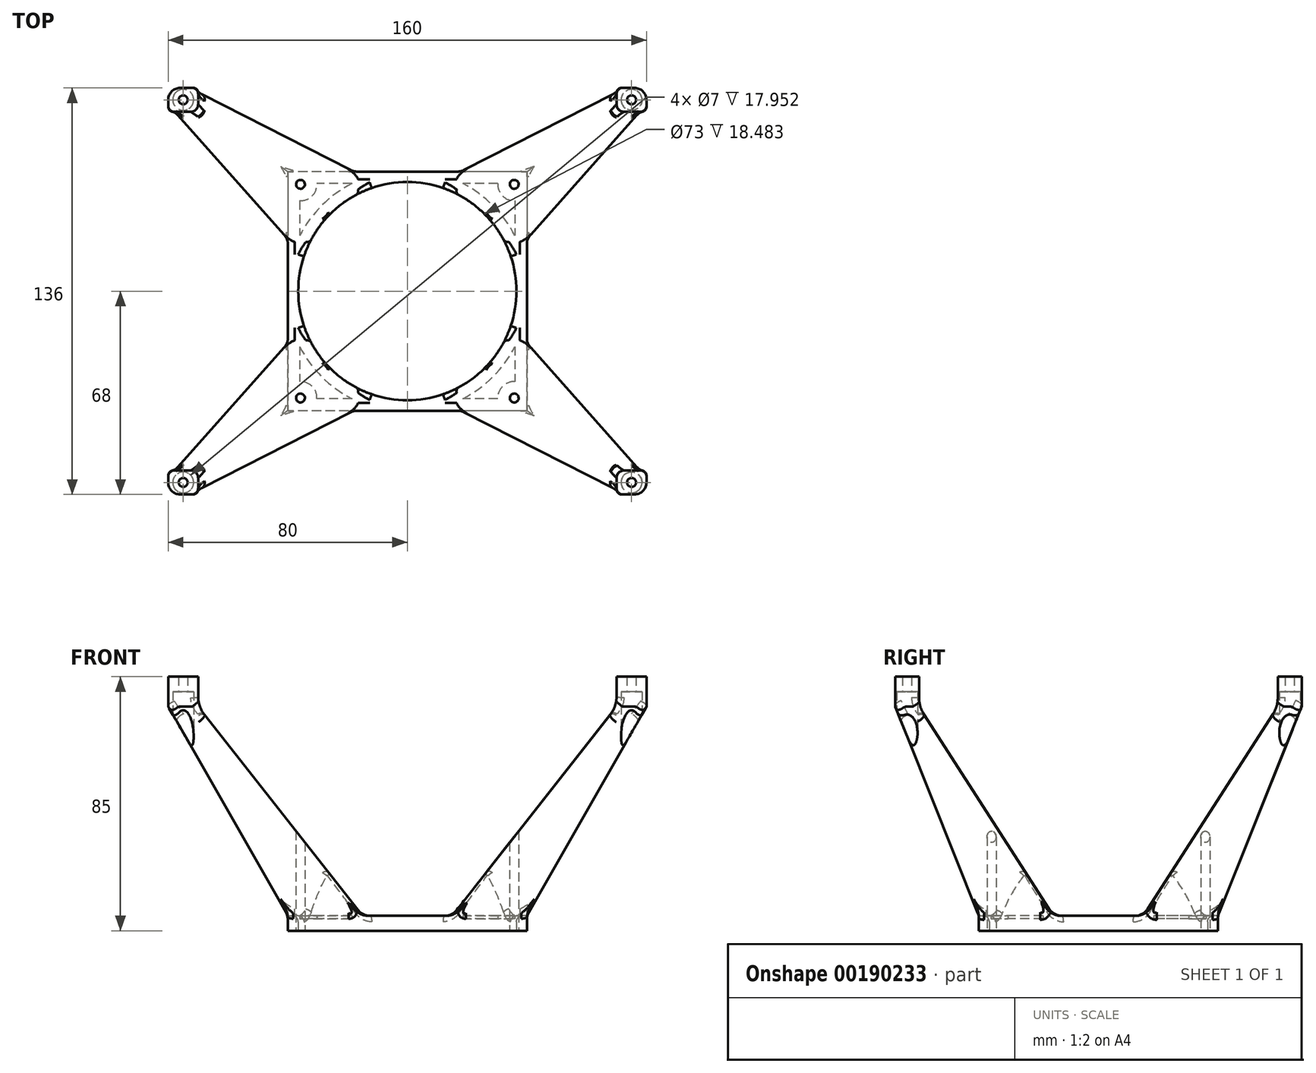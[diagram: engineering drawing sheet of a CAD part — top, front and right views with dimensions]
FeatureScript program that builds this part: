
annotation { "Feature Type Name" : "Feature", "Feature Type Description" : "" }
export const myFeature = defineFeature(function(context is Context, id is Id, definition is map)
    precondition{}
    {
        {
            var Q0;
            Q0=qCreatedBy(makeId("Top.planeOp"),FACE);
            var sketch = newSketch(context, id + "F0", { "sketchPlane" : qUnion([Q0])});
            skLineSegment(sketch, "E0", {"start": v(-35.75, 35.75) * mm, "end": v(35.75, -35.75) * mm, "construction": true});
            skLineSegment(sketch, "E1", {"start": v(35.75, -35.75) * mm, "end": v(-35.75, -35.75) * mm, "construction": true});
            skLineSegment(sketch, "E2", {"start": v(-35.75, -35.75) * mm, "end": v(35.75, 35.75) * mm, "construction": true});
            skLineSegment(sketch, "E3", {"start": v(35.75, 35.75) * mm, "end": v(-35.75, 35.75) * mm, "construction": true});
            skCircle(sketch, "E4", {"center": v(35.75, 35.75) * mm, "radius": 1.5 * mm});
            skCircle(sketch, "E5", {"center": v(-35.75, 35.75) * mm, "radius": 1.5 * mm});
            skCircle(sketch, "E6", {"center": v(-35.75, -35.75) * mm, "radius": 1.5 * mm});
            skCircle(sketch, "E7", {"center": v(35.75, -35.75) * mm, "radius": 1.5 * mm});
            skLineSegment(sketch, "E8.bottom", {"start": v(40, 40) * mm, "end": v(-40, 40) * mm});
            skLineSegment(sketch, "E8.top", {"start": v(40, -40) * mm, "end": v(-40, -40) * mm});
            skLineSegment(sketch, "E8.left", {"start": v(40, 40) * mm, "end": v(40, -40) * mm});
            skLineSegment(sketch, "E8.right", {"start": v(-40, 40) * mm, "end": v(-40, -40) * mm});
            skCircle(sketch, "E9", {"center": v(0, 0) * mm, "radius": 36.5 * mm});
            skSolve(sketch);
        }
        {
            var Q0;
            Q0 = qSketchRegion(id + "F0", true);
            extrude(context, id + "F1", {"entities" : qUnion([Q0]), "depth" : 5 * mm});
        }
        {
            var Q0;
            Q0=makeQuery(id+"F1.opExtrude","CAP_FACE",FACE,{"disambiguationData":[OSD([sQuery(id+"F0.wireOp",EDGE,"E4"),sQuery(id+"F0.wireOp",EDGE,"E5"),sQuery(id+"F0.wireOp",EDGE,"E6"),sQuery(id+"F0.wireOp",EDGE,"E7"),sQuery(id+"F0.wireOp",EDGE,"E8.bottom"),sQuery(id+"F0.wireOp",EDGE,"E8.top"),sQuery(id+"F0.wireOp",EDGE,"E8.left"),sQuery(id+"F0.wireOp",EDGE,"E8.right"),sQuery(id+"F0.wireOp",EDGE,"E9")])],"isStart":false});
            shell(context, id + "F2", {"entities" : qUnion([Q0]), "thickness" : 4 * mm});
        }
        {
            var Q0;
            Q0=qCreatedBy(makeId("Right.planeOp"),FACE);
            var sketch = newSketch(context, id + "F3", { "sketchPlane" : qUnion([Q0])});
            skLineSegment(sketch, "E10", {"start": v(40, 5) * mm, "end": v(68, 75) * mm});
            skLineSegment(sketch, "E11", {"start": v(68, 75) * mm, "end": v(60, 75) * mm, "construction": true});
            skLineSegment(sketch, "E12", {"start": v(58.41, 72.53) * mm, "end": v(15, 5) * mm});
            skLineSegment(sketch, "E13", {"start": v(68, 75) * mm, "end": v(68, 85) * mm});
            skLineSegment(sketch, "E14", {"start": v(68, 85) * mm, "end": v(60, 85) * mm});
            skLineSegment(sketch, "E15", {"start": v(60, 85) * mm, "end": v(60, 77.94) * mm});
            skLineSegment(sketch, "E16", {"start": v(40, 5) * mm, "end": v(15, 5) * mm});
            skPoint(sketch, "E17.visualSharp", {"position": v(60, 75) * mm});
            skArc(sketch, "E17.filletArc", {"start": v(58.41, 72.53) * mm, "mid": v(59.6, 75.12) * mm, "end": v(60, 77.94) * mm});
            skSolve(sketch);
        }
        {
            var Q0;
            Q0 = qSketchRegion(id + "F3", true);
            extrude(context, id + "F4", {"entities" : qUnion([Q0]), "endBound" : BoundingType.SYMMETRIC, "depth" : 160 * mm});
        }
        {
            var Q0;
            Q0=qCreatedBy(makeId("Front.planeOp"),FACE);
            var sketch = newSketch(context, id + "F5", { "sketchPlane" : qUnion([Q0])});
            skLineSegment(sketch, "E18", {"start": v(40, 5) * mm, "end": v(80, 75) * mm});
            skLineSegment(sketch, "E19", {"start": v(80, 75) * mm, "end": v(80, 5) * mm});
            skLineSegment(sketch, "E20", {"start": v(80, 5) * mm, "end": v(40, 5) * mm});
            skLineSegment(sketch, "E21", {"start": v(0, 0) * mm, "end": v(0, 85) * mm, "construction": true});
            skLineSegment(sketch, "E22.MirrorCS", {"start": v(-80, 5) * mm, "end": v(-40, 5) * mm});
            skLineSegment(sketch, "E23.MirrorCS", {"start": v(-80, 75) * mm, "end": v(-80, 5) * mm});
            skLineSegment(sketch, "E24.MirrorCS", {"start": v(-40, 5) * mm, "end": v(-80, 75) * mm});
            skLineSegment(sketch, "E25", {"start": v(70, 85) * mm, "end": v(70, 78.46) * mm});
            skLineSegment(sketch, "E26", {"start": v(67.86, 72.28) * mm, "end": v(15, 5) * mm});
            skLineSegment(sketch, "E27", {"start": v(15, 5) * mm, "end": v(0, 5) * mm});
            skPoint(sketch, "E28.visualSharp", {"position": v(70, 75) * mm});
            skArc(sketch, "E28.filletArc", {"start": v(67.86, 72.28) * mm, "mid": v(69.45, 75.19) * mm, "end": v(70, 78.46) * mm});
            skLineSegment(sketch, "E29", {"start": v(70, 85) * mm, "end": v(0, 85) * mm});
            skLineSegment(sketch, "E30.MirrorCS", {"start": v(-15, 5) * mm, "end": v(0, 5) * mm});
            skLineSegment(sketch, "E31.MirrorCS", {"start": v(-67.86, 72.28) * mm, "end": v(-15, 5) * mm});
            skArc(sketch, "E32.MirrorCS", {"start": v(-67.86, 72.28) * mm, "mid": v(-69.45, 75.19) * mm, "end": v(-70, 78.46) * mm});
            skLineSegment(sketch, "E33.MirrorCS", {"start": v(-70, 85) * mm, "end": v(-70, 78.46) * mm});
            skLineSegment(sketch, "E34.MirrorCS", {"start": v(-70, 85) * mm, "end": v(0, 85) * mm});
            skSolve(sketch);
        }
        {
            var Q0;
            Q0 = qSketchRegion(id + "F5", true);
            extrude(context, id + "F6", {"entities" : qUnion([Q0]), "operationType" : NewBodyOperationType.REMOVE, "endBound" : BoundingType.THROUGH_ALL, "oppositeDirection" : true, "depth" : 25 * mm, "hasSecondDirection" : true, "secondDirectionBound" : SecondDirectionBoundingType.THROUGH_ALL, "secondDirectionOppositeDirection" : false, "secondDirectionDepth" : 25 * mm});
        }
        {
            var Q0;
            Q0=makeQuery(id+"F6.boolean.opBoolean","SPLIT",BODY,{"disambiguationData":[OD(1.0)],"derivedFrom":makeQuery(id+"F4.opExtrude","SWEPT_BODY",BODY,{"disambiguationData":[OSD([sQuery(id+"F3.wireOp",EDGE,"E10"),sQuery(id+"F3.wireOp",EDGE,"E12"),sQuery(id+"F3.wireOp",EDGE,"E13"),sQuery(id+"F3.wireOp",EDGE,"E14"),sQuery(id+"F3.wireOp",EDGE,"E15"),sQuery(id+"F3.wireOp",EDGE,"E16"),sQuery(id+"F3.wireOp",EDGE,"E17.filletArc")])]})});
            var Q1;
            Q1=makeQuery(id+"F6.boolean.opBoolean","SPLIT",BODY,{"disambiguationData":[OD(0.0)],"derivedFrom":makeQuery(id+"F4.opExtrude","SWEPT_BODY",BODY,{"disambiguationData":[OSD([sQuery(id+"F3.wireOp",EDGE,"E10"),sQuery(id+"F3.wireOp",EDGE,"E12"),sQuery(id+"F3.wireOp",EDGE,"E13"),sQuery(id+"F3.wireOp",EDGE,"E14"),sQuery(id+"F3.wireOp",EDGE,"E15"),sQuery(id+"F3.wireOp",EDGE,"E16"),sQuery(id+"F3.wireOp",EDGE,"E17.filletArc")])]})});
            var Q2;
            Q2=qCreatedBy(makeId("Front.planeOp"),FACE);
            mirror(context, id + "F7", {"operationType" : NewBodyOperationType.ADD, "entities" : qUnion([Q0, Q1]), "mirrorPlane" : qUnion([Q2])});
        }
        {
            var Q0;
            Q0=qCreatedBy(makeId("Top.planeOp"),FACE);
            var sketch = newSketch(context, id + "F8", { "sketchPlane" : qUnion([Q0])});
            skCircle(sketch, "E35", {"center": v(0, 0) * mm, "radius": 36.5 * mm});
            skCircle(sketch, "E36", {"center": v(35.75, -35.75) * mm, "radius": 1.5 * mm});
            skCircle(sketch, "E37", {"center": v(-35.75, -35.75) * mm, "radius": 1.5 * mm});
            skCircle(sketch, "E38", {"center": v(-35.75, 35.75) * mm, "radius": 1.5 * mm});
            skCircle(sketch, "E39", {"center": v(35.75, 35.75) * mm, "radius": 1.5 * mm});
            skSolve(sketch);
        }
        {
            var Q0;
            Q0 = qSketchRegion(id + "F8", true);
            extrude(context, id + "F9", {"entities" : qUnion([Q0]), "operationType" : NewBodyOperationType.REMOVE, "endBound" : BoundingType.THROUGH_ALL, "depth" : 25 * mm});
        }
        {
            var Q0;
            Q0=makeQuery(id+"F6.boolean.opBoolean","INTERSECT",EDGE,{"derivedFrom":[makeQuery(id+"F4.opExtrude","SWEPT_FACE",FACE,{"disambiguationData":[OSD([sQuery(id+"F3.wireOp",EDGE,"E12")])]}),makeQuery(id+"F6.opExtrude","SWEPT_FACE",FACE,{"disambiguationData":[OSD([sQuery(id+"F5.wireOp",EDGE,"E26")])]})]});
            var Q1;
            Q1=makeQuery(id+"F7.opPattern","COPY",EDGE,{"derivedFrom":makeQuery(id+"F6.boolean.opBoolean","INTERSECT",EDGE,{"derivedFrom":[makeQuery(id+"F4.opExtrude","SWEPT_FACE",FACE,{"disambiguationData":[OSD([sQuery(id+"F3.wireOp",EDGE,"E12")])]}),makeQuery(id+"F6.opExtrude","SWEPT_FACE",FACE,{"disambiguationData":[OSD([sQuery(id+"F5.wireOp",EDGE,"E26")])]})]}),"instanceName":"1"});
            var Q2;
            Q2=makeQuery(id+"F7.opPattern","COPY",EDGE,{"derivedFrom":makeQuery(id+"F6.boolean.opBoolean","INTERSECT",EDGE,{"derivedFrom":[makeQuery(id+"F4.opExtrude","SWEPT_FACE",FACE,{"disambiguationData":[OSD([sQuery(id+"F3.wireOp",EDGE,"E12")])]}),makeQuery(id+"F6.opExtrude","SWEPT_FACE",FACE,{"disambiguationData":[OSD([sQuery(id+"F5.wireOp",EDGE,"E31.MirrorCS")])]})]}),"instanceName":"1"});
            var Q3;
            Q3=makeQuery(id+"F6.boolean.opBoolean","INTERSECT",EDGE,{"derivedFrom":[makeQuery(id+"F4.opExtrude","SWEPT_FACE",FACE,{"disambiguationData":[OSD([sQuery(id+"F3.wireOp",EDGE,"E12")])]}),makeQuery(id+"F6.opExtrude","SWEPT_FACE",FACE,{"disambiguationData":[OSD([sQuery(id+"F5.wireOp",EDGE,"E31.MirrorCS")])]})]});
            var Q4;
            Q4=makeQuery(id+"F6.boolean.opBoolean","INTERSECT",EDGE,{"derivedFrom":[makeQuery(id+"F4.opExtrude","SWEPT_FACE",FACE,{"disambiguationData":[OSD([sQuery(id+"F3.wireOp",EDGE,"E12")])]}),makeQuery(id+"F6.opExtrude","SWEPT_FACE",FACE,{"disambiguationData":[OSD([sQuery(id+"F5.wireOp",EDGE,"E24.MirrorCS")])]})]});
            var Q5;
            Q5=makeQuery(id+"F6.boolean.opBoolean","INTERSECT",EDGE,{"derivedFrom":[makeQuery(id+"F4.opExtrude","SWEPT_FACE",FACE,{"disambiguationData":[OSD([sQuery(id+"F3.wireOp",EDGE,"E10")])]}),makeQuery(id+"F6.opExtrude","SWEPT_FACE",FACE,{"disambiguationData":[OSD([sQuery(id+"F5.wireOp",EDGE,"E31.MirrorCS")])]})]});
            var Q6;
            Q6=makeQuery(id+"F6.boolean.opBoolean","INTERSECT",EDGE,{"derivedFrom":[makeQuery(id+"F4.opExtrude","SWEPT_FACE",FACE,{"disambiguationData":[OSD([sQuery(id+"F3.wireOp",EDGE,"E10")])]}),makeQuery(id+"F6.opExtrude","SWEPT_FACE",FACE,{"disambiguationData":[OSD([sQuery(id+"F5.wireOp",EDGE,"E26")])]})]});
            var Q7;
            Q7=makeQuery(id+"F6.boolean.opBoolean","INTERSECT",EDGE,{"derivedFrom":[makeQuery(id+"F4.opExtrude","SWEPT_FACE",FACE,{"disambiguationData":[OSD([sQuery(id+"F3.wireOp",EDGE,"E12")])]}),makeQuery(id+"F6.opExtrude","SWEPT_FACE",FACE,{"disambiguationData":[OSD([sQuery(id+"F5.wireOp",EDGE,"E18")])]})]});
            var Q8;
            Q8=makeQuery(id+"F7.opPattern","COPY",EDGE,{"derivedFrom":makeQuery(id+"F6.boolean.opBoolean","INTERSECT",EDGE,{"derivedFrom":[makeQuery(id+"F4.opExtrude","SWEPT_FACE",FACE,{"disambiguationData":[OSD([sQuery(id+"F3.wireOp",EDGE,"E10")])]}),makeQuery(id+"F6.opExtrude","SWEPT_FACE",FACE,{"disambiguationData":[OSD([sQuery(id+"F5.wireOp",EDGE,"E31.MirrorCS")])]})]}),"instanceName":"1"});
            var Q9;
            Q9=makeQuery(id+"F7.opPattern","COPY",EDGE,{"derivedFrom":makeQuery(id+"F6.boolean.opBoolean","INTERSECT",EDGE,{"derivedFrom":[makeQuery(id+"F4.opExtrude","SWEPT_FACE",FACE,{"disambiguationData":[OSD([sQuery(id+"F3.wireOp",EDGE,"E12")])]}),makeQuery(id+"F6.opExtrude","SWEPT_FACE",FACE,{"disambiguationData":[OSD([sQuery(id+"F5.wireOp",EDGE,"E24.MirrorCS")])]})]}),"instanceName":"1"});
            var Q10;
            Q10=makeQuery(id+"F7.opPattern","COPY",EDGE,{"derivedFrom":makeQuery(id+"F6.boolean.opBoolean","INTERSECT",EDGE,{"derivedFrom":[makeQuery(id+"F4.opExtrude","SWEPT_FACE",FACE,{"disambiguationData":[OSD([sQuery(id+"F3.wireOp",EDGE,"E10")])]}),makeQuery(id+"F6.opExtrude","SWEPT_FACE",FACE,{"disambiguationData":[OSD([sQuery(id+"F5.wireOp",EDGE,"E26")])]})]}),"instanceName":"1"});
            var Q11;
            Q11=makeQuery(id+"F7.opPattern","COPY",EDGE,{"derivedFrom":makeQuery(id+"F6.boolean.opBoolean","INTERSECT",EDGE,{"derivedFrom":[makeQuery(id+"F4.opExtrude","SWEPT_FACE",FACE,{"disambiguationData":[OSD([sQuery(id+"F3.wireOp",EDGE,"E12")])]}),makeQuery(id+"F6.opExtrude","SWEPT_FACE",FACE,{"disambiguationData":[OSD([sQuery(id+"F5.wireOp",EDGE,"E18")])]})]}),"instanceName":"1"});
            var Q12;
            Q12=makeQuery(id+"F6.boolean.opBoolean","INTERSECT",EDGE,{"derivedFrom":[makeQuery(id+"F4.opExtrude","SWEPT_FACE",FACE,{"disambiguationData":[OSD([sQuery(id+"F3.wireOp",EDGE,"E10")])]}),makeQuery(id+"F6.opExtrude","SWEPT_FACE",FACE,{"disambiguationData":[OSD([sQuery(id+"F5.wireOp",EDGE,"E24.MirrorCS")])]})]});
            var Q13;
            Q13=makeQuery(id+"F7.opPattern","COPY",EDGE,{"derivedFrom":makeQuery(id+"F6.boolean.opBoolean","INTERSECT",EDGE,{"derivedFrom":[makeQuery(id+"F4.opExtrude","SWEPT_FACE",FACE,{"disambiguationData":[OSD([sQuery(id+"F3.wireOp",EDGE,"E10")])]}),makeQuery(id+"F6.opExtrude","SWEPT_FACE",FACE,{"disambiguationData":[OSD([sQuery(id+"F5.wireOp",EDGE,"E24.MirrorCS")])]})]}),"instanceName":"1"});
            var Q14;
            Q14=makeQuery(id+"F7.opPattern","COPY",EDGE,{"derivedFrom":makeQuery(id+"F6.boolean.opBoolean","INTERSECT",EDGE,{"derivedFrom":[makeQuery(id+"F4.opExtrude","SWEPT_FACE",FACE,{"disambiguationData":[OSD([sQuery(id+"F3.wireOp",EDGE,"E10")])]}),makeQuery(id+"F6.opExtrude","SWEPT_FACE",FACE,{"disambiguationData":[OSD([sQuery(id+"F5.wireOp",EDGE,"E18")])]})]}),"instanceName":"1"});
            var Q15;
            Q15=makeQuery(id+"F6.boolean.opBoolean","INTERSECT",EDGE,{"derivedFrom":[makeQuery(id+"F4.opExtrude","SWEPT_FACE",FACE,{"disambiguationData":[OSD([sQuery(id+"F3.wireOp",EDGE,"E10")])]}),makeQuery(id+"F6.opExtrude","SWEPT_FACE",FACE,{"disambiguationData":[OSD([sQuery(id+"F5.wireOp",EDGE,"E18")])]})]});
            fillet(context, id + "F10", {"entities" : qUnion([Q0, Q1, Q2, Q3, Q4, Q5, Q6, Q7, Q8, Q9, Q10, Q11, Q12, Q13, Q14, Q15]), "radius" : 2.5 * mm, "tangentPropagation" : true, "allowEdgeOverflow" : false});
        }
        {
            var Q0;
            Q0=makeQuery(id+"F7.boolean.opBoolean","MERGE",EDGE,{"derivedFrom":[makeQuery(id+"F1.opExtrude","CAP_EDGE",EDGE,{"disambiguationData":[OSD([sQuery(id+"F0.wireOp",EDGE,"E8.left")])],"isStart":false}),makeQuery(id+"F7.opPattern","COPY",EDGE,{"derivedFrom":makeQuery(id+"F6.boolean.opBoolean","COPY",EDGE,{"derivedFrom":makeQuery(id+"F6.opExtrude","SWEPT_EDGE",EDGE,{"disambiguationData":[OSD([sQuery(id+"F5.wireOp",EDGE,"E18"),sQuery(id+"F5.wireOp",EDGE,"E20")])]})}),"instanceName":"1"})]});
            var Q1;
            Q1=makeQuery(id+"F7.boolean.opBoolean","MERGE",EDGE,{"derivedFrom":[makeQuery(id+"F1.opExtrude","CAP_EDGE",EDGE,{"disambiguationData":[OSD([sQuery(id+"F0.wireOp",EDGE,"E8.left")])],"isStart":false}),makeQuery(id+"F6.boolean.opBoolean","COPY",EDGE,{"derivedFrom":makeQuery(id+"F6.opExtrude","SWEPT_EDGE",EDGE,{"disambiguationData":[OSD([sQuery(id+"F5.wireOp",EDGE,"E18"),sQuery(id+"F5.wireOp",EDGE,"E20")])]})})]});
            var Q2;
            {var subQ0=sQuery(id+"F3.wireOp",EDGE,"E10");var subQ1=sQuery(id+"F3.wireOp",EDGE,"E16");Q2=makeQuery(id+"F7.boolean.opBoolean","MERGE",EDGE,{"derivedFrom":[makeQuery(id+"F1.opExtrude","CAP_EDGE",EDGE,{"disambiguationData":[OSD([sQuery(id+"F0.wireOp",EDGE,"E8.top")])],"isStart":false}),makeQuery(id+"F7.opPattern","COPY",EDGE,{"derivedFrom":makeQuery(id+"F6.boolean.opBoolean","SPLIT",EDGE,{"disambiguationData":[TD([makeQuery(id+"F6.opExtrude","SWEPT_FACE",FACE,{"disambiguationData":[OSD([sQuery(id+"F5.wireOp",EDGE,"E18")])]})])],"derivedFrom":makeQuery(id+"F4.opExtrude","SWEPT_EDGE",EDGE,{"disambiguationData":[OSD([subQ0,subQ1])]})}),"instanceName":"1"})]});}
            var Q3;
            {var subQ0=sQuery(id+"F3.wireOp",EDGE,"E10");var subQ1=sQuery(id+"F3.wireOp",EDGE,"E16");Q3=makeQuery(id+"F7.boolean.opBoolean","MERGE",EDGE,{"derivedFrom":[makeQuery(id+"F1.opExtrude","CAP_EDGE",EDGE,{"disambiguationData":[OSD([sQuery(id+"F0.wireOp",EDGE,"E8.top")])],"isStart":false}),makeQuery(id+"F7.opPattern","COPY",EDGE,{"derivedFrom":makeQuery(id+"F6.boolean.opBoolean","SPLIT",EDGE,{"disambiguationData":[TD([makeQuery(id+"F6.opExtrude","SWEPT_FACE",FACE,{"disambiguationData":[OSD([sQuery(id+"F5.wireOp",EDGE,"E24.MirrorCS")])]})])],"derivedFrom":makeQuery(id+"F4.opExtrude","SWEPT_EDGE",EDGE,{"disambiguationData":[OSD([subQ0,subQ1])]})}),"instanceName":"1"})]});}
            var Q4;
            Q4=makeQuery(id+"F7.boolean.opBoolean","MERGE",EDGE,{"derivedFrom":[makeQuery(id+"F1.opExtrude","CAP_EDGE",EDGE,{"disambiguationData":[OSD([sQuery(id+"F0.wireOp",EDGE,"E8.right")])],"isStart":false}),makeQuery(id+"F7.opPattern","COPY",EDGE,{"derivedFrom":makeQuery(id+"F6.boolean.opBoolean","COPY",EDGE,{"derivedFrom":makeQuery(id+"F6.opExtrude","SWEPT_EDGE",EDGE,{"disambiguationData":[OSD([sQuery(id+"F5.wireOp",EDGE,"E22.MirrorCS"),sQuery(id+"F5.wireOp",EDGE,"E24.MirrorCS")])]})}),"instanceName":"1"})]});
            var Q5;
            Q5=makeQuery(id+"F7.boolean.opBoolean","MERGE",EDGE,{"derivedFrom":[makeQuery(id+"F1.opExtrude","CAP_EDGE",EDGE,{"disambiguationData":[OSD([sQuery(id+"F0.wireOp",EDGE,"E8.right")])],"isStart":false}),makeQuery(id+"F6.boolean.opBoolean","COPY",EDGE,{"derivedFrom":makeQuery(id+"F6.opExtrude","SWEPT_EDGE",EDGE,{"disambiguationData":[OSD([sQuery(id+"F5.wireOp",EDGE,"E22.MirrorCS"),sQuery(id+"F5.wireOp",EDGE,"E24.MirrorCS")])]})})]});
            var Q6;
            {var subQ0=sQuery(id+"F3.wireOp",EDGE,"E10");var subQ1=sQuery(id+"F3.wireOp",EDGE,"E16");Q6=makeQuery(id+"F7.boolean.opBoolean","MERGE",EDGE,{"derivedFrom":[makeQuery(id+"F1.opExtrude","CAP_EDGE",EDGE,{"disambiguationData":[OSD([sQuery(id+"F0.wireOp",EDGE,"E8.bottom")])],"isStart":false}),makeQuery(id+"F6.boolean.opBoolean","SPLIT",EDGE,{"disambiguationData":[TD([makeQuery(id+"F6.opExtrude","SWEPT_FACE",FACE,{"disambiguationData":[OSD([sQuery(id+"F5.wireOp",EDGE,"E24.MirrorCS")])]})])],"derivedFrom":makeQuery(id+"F4.opExtrude","SWEPT_EDGE",EDGE,{"disambiguationData":[OSD([subQ0,subQ1])]})})]});}
            var Q7;
            {var subQ0=sQuery(id+"F3.wireOp",EDGE,"E10");var subQ1=sQuery(id+"F3.wireOp",EDGE,"E16");Q7=makeQuery(id+"F7.boolean.opBoolean","MERGE",EDGE,{"derivedFrom":[makeQuery(id+"F1.opExtrude","CAP_EDGE",EDGE,{"disambiguationData":[OSD([sQuery(id+"F0.wireOp",EDGE,"E8.bottom")])],"isStart":false}),makeQuery(id+"F6.boolean.opBoolean","SPLIT",EDGE,{"disambiguationData":[TD([makeQuery(id+"F6.opExtrude","SWEPT_FACE",FACE,{"disambiguationData":[OSD([sQuery(id+"F5.wireOp",EDGE,"E18")])]})])],"derivedFrom":makeQuery(id+"F4.opExtrude","SWEPT_EDGE",EDGE,{"disambiguationData":[OSD([subQ0,subQ1])]})})]});}
            fillet(context, id + "F11", {"entities" : qUnion([Q0, Q1, Q2, Q3, Q4, Q5, Q6, Q7]), "radius" : 5 * mm, "tangentPropagation" : true, "allowEdgeOverflow" : false});
        }
        {
            var Q0;
            Q0=qCreatedBy(makeId("Top.planeOp"),FACE);
            var sketch = newSketch(context, id + "F12", { "sketchPlane" : qUnion([Q0])});
            skLineSegment(sketch, "E40", {"start": v(-80, 60) * mm, "end": v(-70, 68) * mm, "construction": true});
            skLineSegment(sketch, "E41", {"start": v(70, 68) * mm, "end": v(80, 60) * mm, "construction": true});
            skCircle(sketch, "E42", {"center": v(75, 64) * mm, "radius": 1.5 * mm});
            skCircle(sketch, "E43", {"center": v(-75, 64) * mm, "radius": 1.5 * mm});
            skLineSegment(sketch, "E44.MirrorCS", {"start": v(70, -68) * mm, "end": v(80, -60) * mm, "construction": true});
            skLineSegment(sketch, "E45.MirrorCS", {"start": v(-80, -60) * mm, "end": v(-70, -68) * mm, "construction": true});
            skCircle(sketch, "E46.MirrorC", {"center": v(75, -64) * mm, "radius": 1.5 * mm});
            skCircle(sketch, "E47.MirrorC", {"center": v(-75, -64) * mm, "radius": 1.5 * mm});
            skSolve(sketch);
        }
        {
            var Q0;
            Q0 = qSketchRegion(id + "F12", true);
            extrude(context, id + "F13", {"entities" : qUnion([Q0]), "operationType" : NewBodyOperationType.REMOVE, "endBound" : BoundingType.THROUGH_ALL, "depth" : 25 * mm});
        }
        {
            var Q0;
            Q0=qCreatedBy(makeId("Top.planeOp"),FACE);
            var sketch = newSketch(context, id + "F14", { "sketchPlane" : qUnion([Q0])});
            skCircle(sketch, "E48", {"center": v(-75, 64) * mm, "radius": 3.5 * mm});
            skCircle(sketch, "E49", {"center": v(75, 64) * mm, "radius": 3.5 * mm});
            skCircle(sketch, "E50", {"center": v(75, -64) * mm, "radius": 3.5 * mm});
            skCircle(sketch, "E51", {"center": v(-75, -64) * mm, "radius": 3.5 * mm});
            skSolve(sketch);
        }
        {
            var Q0;
            Q0 = qSketchRegion(id + "F14", true);
            extrude(context, id + "F15", {"entities" : qUnion([Q0]), "operationType" : NewBodyOperationType.REMOVE, "depth" : 80 * mm});
        }
        {
            var Q0;
            Q0=makeQuery(id+"F7.opPattern","COPY",EDGE,{"derivedFrom":makeQuery(id+"F4.opExtrude","CAP_EDGE",EDGE,{"disambiguationData":[OSD([sQuery(id+"F3.wireOp",EDGE,"E13")])],"isStart":true}),"instanceName":"1"});
            var Q1;
            Q1=makeQuery(id+"F4.opExtrude","CAP_EDGE",EDGE,{"disambiguationData":[OSD([sQuery(id+"F3.wireOp",EDGE,"E13")])],"isStart":true});
            var Q2;
            Q2=makeQuery(id+"F4.opExtrude","CAP_EDGE",EDGE,{"disambiguationData":[OSD([sQuery(id+"F3.wireOp",EDGE,"E13")])],"isStart":false});
            var Q3;
            Q3=makeQuery(id+"F7.opPattern","COPY",EDGE,{"derivedFrom":makeQuery(id+"F4.opExtrude","CAP_EDGE",EDGE,{"disambiguationData":[OSD([sQuery(id+"F3.wireOp",EDGE,"E13")])],"isStart":false}),"instanceName":"1"});
            fillet(context, id + "F16", {"entities" : qUnion([Q0, Q1, Q2, Q3]), "radius" : 4 * mm, "tangentPropagation" : true, "allowEdgeOverflow" : false});
        }
        {
            var Q0;
            Q0=makeQuery(id+"F7.opPattern","COPY",EDGE,{"derivedFrom":makeQuery(id+"F4.opExtrude","CAP_EDGE",EDGE,{"disambiguationData":[OSD([sQuery(id+"F3.wireOp",EDGE,"E15")])],"isStart":false}),"instanceName":"1"});
            var Q1;
            Q1=makeQuery(id+"F4.opExtrude","CAP_EDGE",EDGE,{"disambiguationData":[OSD([sQuery(id+"F3.wireOp",EDGE,"E15")])],"isStart":false});
            var Q2;
            Q2=makeQuery(id+"F7.opPattern","COPY",EDGE,{"derivedFrom":makeQuery(id+"F6.boolean.opBoolean","INTERSECT",EDGE,{"derivedFrom":[makeQuery(id+"F4.opExtrude","SWEPT_FACE",FACE,{"disambiguationData":[OSD([sQuery(id+"F3.wireOp",EDGE,"E13")])]}),makeQuery(id+"F6.opExtrude","SWEPT_FACE",FACE,{"disambiguationData":[OSD([sQuery(id+"F5.wireOp",EDGE,"E25")])]})]}),"instanceName":"1"});
            var Q3;
            Q3=makeQuery(id+"F6.boolean.opBoolean","INTERSECT",EDGE,{"derivedFrom":[makeQuery(id+"F4.opExtrude","SWEPT_FACE",FACE,{"disambiguationData":[OSD([sQuery(id+"F3.wireOp",EDGE,"E13")])]}),makeQuery(id+"F6.opExtrude","SWEPT_FACE",FACE,{"disambiguationData":[OSD([sQuery(id+"F5.wireOp",EDGE,"E25")])]})]});
            var Q4;
            Q4=makeQuery(id+"F4.opExtrude","CAP_EDGE",EDGE,{"disambiguationData":[OSD([sQuery(id+"F3.wireOp",EDGE,"E15")])],"isStart":true});
            var Q5;
            Q5=makeQuery(id+"F6.boolean.opBoolean","INTERSECT",EDGE,{"derivedFrom":[makeQuery(id+"F4.opExtrude","SWEPT_FACE",FACE,{"disambiguationData":[OSD([sQuery(id+"F3.wireOp",EDGE,"E13")])]}),makeQuery(id+"F6.opExtrude","SWEPT_FACE",FACE,{"disambiguationData":[OSD([sQuery(id+"F5.wireOp",EDGE,"E33.MirrorCS")])]})]});
            var Q6;
            Q6=makeQuery(id+"F7.opPattern","COPY",EDGE,{"derivedFrom":makeQuery(id+"F6.boolean.opBoolean","INTERSECT",EDGE,{"derivedFrom":[makeQuery(id+"F4.opExtrude","SWEPT_FACE",FACE,{"disambiguationData":[OSD([sQuery(id+"F3.wireOp",EDGE,"E13")])]}),makeQuery(id+"F6.opExtrude","SWEPT_FACE",FACE,{"disambiguationData":[OSD([sQuery(id+"F5.wireOp",EDGE,"E33.MirrorCS")])]})]}),"instanceName":"1"});
            var Q7;
            Q7=makeQuery(id+"F7.opPattern","COPY",EDGE,{"derivedFrom":makeQuery(id+"F4.opExtrude","CAP_EDGE",EDGE,{"disambiguationData":[OSD([sQuery(id+"F3.wireOp",EDGE,"E15")])],"isStart":true}),"instanceName":"1"});
            fillet(context, id + "F17", {"entities" : qUnion([Q0, Q1, Q2, Q3, Q4, Q5, Q6, Q7]), "radius" : 2 * mm, "tangentPropagation" : true, "allowEdgeOverflow" : false});
        }
        {
            var Q0;
            {var subQ0=makeQuery(id+"F4.opExtrude","SWEPT_FACE",FACE,{"disambiguationData":[OSD([sQuery(id+"F3.wireOp",EDGE,"E16")])]});var subQ1=makeQuery(id+"F4.opExtrude","SWEPT_FACE",FACE,{"disambiguationData":[OSD([sQuery(id+"F3.wireOp",EDGE,"E12")])]});var subQ2=sQuery(id+"F0.wireOp",EDGE,"E9");var subQ4=makeQuery(id+"F6.opExtrude","SWEPT_FACE",FACE,{"disambiguationData":[OSD([sQuery(id+"F5.wireOp",EDGE,"E24.MirrorCS")])]});Q0=makeQuery(id+"F7.boolean.opBoolean","SPLIT",EDGE,{"disambiguationData":[TD([makeQuery(id+"F1.opExtrude","CAP_FACE",FACE,{"disambiguationData":[OSD([sQuery(id+"F0.wireOp",EDGE,"E4"),sQuery(id+"F0.wireOp",EDGE,"E5"),sQuery(id+"F0.wireOp",EDGE,"E6"),sQuery(id+"F0.wireOp",EDGE,"E7"),sQuery(id+"F0.wireOp",EDGE,"E8.bottom"),sQuery(id+"F0.wireOp",EDGE,"E8.top"),sQuery(id+"F0.wireOp",EDGE,"E8.left"),sQuery(id+"F0.wireOp",EDGE,"E8.right"),subQ2])],"isStart":false}),makeQuery(id+"F1.opExtrude","SWEPT_FACE",FACE,{"disambiguationData":[OSD([subQ2])]}),subQ1,subQ0,makeQuery(id+"F7.opPattern","COPY",FACE,{"derivedFrom":makeQuery(id+"F6.boolean.opBoolean","SPLIT",FACE,{"disambiguationData":[TD([subQ4])],"derivedFrom":subQ1}),"instanceName":"1"}),makeQuery(id+"F7.opPattern","COPY",FACE,{"derivedFrom":makeQuery(id+"F6.boolean.opBoolean","SPLIT",FACE,{"disambiguationData":[TD([subQ4])],"derivedFrom":subQ0}),"instanceName":"1"})])],"derivedFrom":makeQuery(id+"F1.opExtrude","CAP_EDGE",EDGE,{"disambiguationData":[OSD([subQ2])],"isStart":false})});}
            var Q1;
            {var subQ0=sQuery(id+"F0.wireOp",EDGE,"E9");var subQ1=makeQuery(id+"F6.opExtrude","SWEPT_FACE",FACE,{"disambiguationData":[OSD([sQuery(id+"F5.wireOp",EDGE,"E31.MirrorCS")])]});var subQ2=makeQuery(id+"F6.opExtrude","SWEPT_FACE",FACE,{"disambiguationData":[OSD([sQuery(id+"F5.wireOp",EDGE,"E26")])]});var subQ5=makeQuery(id+"F4.opExtrude","SWEPT_FACE",FACE,{"disambiguationData":[OSD([sQuery(id+"F3.wireOp",EDGE,"E16")])]});Q1=makeQuery(id+"F7.boolean.opBoolean","SPLIT",EDGE,{"disambiguationData":[TD([makeQuery(id+"F1.opExtrude","CAP_FACE",FACE,{"disambiguationData":[OSD([sQuery(id+"F0.wireOp",EDGE,"E4"),sQuery(id+"F0.wireOp",EDGE,"E5"),sQuery(id+"F0.wireOp",EDGE,"E6"),sQuery(id+"F0.wireOp",EDGE,"E7"),sQuery(id+"F0.wireOp",EDGE,"E8.bottom"),sQuery(id+"F0.wireOp",EDGE,"E8.top"),sQuery(id+"F0.wireOp",EDGE,"E8.left"),sQuery(id+"F0.wireOp",EDGE,"E8.right"),subQ0])],"isStart":false}),makeQuery(id+"F1.opExtrude","SWEPT_FACE",FACE,{"disambiguationData":[OSD([subQ0])]}),makeQuery(id+"F7.opPattern","COPY",FACE,{"derivedFrom":makeQuery(id+"F6.boolean.opBoolean","COPY",FACE,{"derivedFrom":subQ2}),"instanceName":"1"}),makeQuery(id+"F7.opPattern","COPY",FACE,{"derivedFrom":makeQuery(id+"F6.boolean.opBoolean","COPY",FACE,{"derivedFrom":subQ1}),"instanceName":"1"}),makeQuery(id+"F7.opPattern","COPY",FACE,{"derivedFrom":makeQuery(id+"F6.boolean.opBoolean","SPLIT",FACE,{"disambiguationData":[TD([makeQuery(id+"F6.opExtrude","SWEPT_FACE",FACE,{"disambiguationData":[OSD([sQuery(id+"F5.wireOp",EDGE,"E18")])]})])],"derivedFrom":subQ5}),"instanceName":"1"}),makeQuery(id+"F7.opPattern","COPY",FACE,{"derivedFrom":makeQuery(id+"F6.boolean.opBoolean","SPLIT",FACE,{"disambiguationData":[TD([makeQuery(id+"F6.opExtrude","SWEPT_FACE",FACE,{"disambiguationData":[OSD([sQuery(id+"F5.wireOp",EDGE,"E24.MirrorCS")])]})])],"derivedFrom":subQ5}),"instanceName":"1"})])],"derivedFrom":makeQuery(id+"F1.opExtrude","CAP_EDGE",EDGE,{"disambiguationData":[OSD([subQ0])],"isStart":false})});}
            var Q2;
            {var subQ0=makeQuery(id+"F4.opExtrude","SWEPT_FACE",FACE,{"disambiguationData":[OSD([sQuery(id+"F3.wireOp",EDGE,"E16")])]});var subQ1=makeQuery(id+"F6.opExtrude","SWEPT_FACE",FACE,{"disambiguationData":[OSD([sQuery(id+"F5.wireOp",EDGE,"E18")])]});var subQ3=makeQuery(id+"F4.opExtrude","SWEPT_FACE",FACE,{"disambiguationData":[OSD([sQuery(id+"F3.wireOp",EDGE,"E12")])]});var subQ4=sQuery(id+"F0.wireOp",EDGE,"E9");Q2=makeQuery(id+"F7.boolean.opBoolean","SPLIT",EDGE,{"disambiguationData":[TD([makeQuery(id+"F1.opExtrude","CAP_FACE",FACE,{"disambiguationData":[OSD([sQuery(id+"F0.wireOp",EDGE,"E4"),sQuery(id+"F0.wireOp",EDGE,"E5"),sQuery(id+"F0.wireOp",EDGE,"E6"),sQuery(id+"F0.wireOp",EDGE,"E7"),sQuery(id+"F0.wireOp",EDGE,"E8.bottom"),sQuery(id+"F0.wireOp",EDGE,"E8.top"),sQuery(id+"F0.wireOp",EDGE,"E8.left"),sQuery(id+"F0.wireOp",EDGE,"E8.right"),subQ4])],"isStart":false}),makeQuery(id+"F1.opExtrude","SWEPT_FACE",FACE,{"disambiguationData":[OSD([subQ4])]}),subQ3,subQ0,makeQuery(id+"F7.opPattern","COPY",FACE,{"derivedFrom":makeQuery(id+"F6.boolean.opBoolean","SPLIT",FACE,{"disambiguationData":[TD([subQ1])],"derivedFrom":subQ3}),"instanceName":"1"}),makeQuery(id+"F7.opPattern","COPY",FACE,{"derivedFrom":makeQuery(id+"F6.boolean.opBoolean","SPLIT",FACE,{"disambiguationData":[TD([subQ1])],"derivedFrom":subQ0}),"instanceName":"1"})])],"derivedFrom":makeQuery(id+"F1.opExtrude","CAP_EDGE",EDGE,{"disambiguationData":[OSD([subQ4])],"isStart":false})});}
            var Q3;
            {var subQ0=sQuery(id+"F0.wireOp",EDGE,"E9");Q3=makeQuery(id+"F7.boolean.opBoolean","SPLIT",EDGE,{"disambiguationData":[TD([makeQuery(id+"F1.opExtrude","CAP_FACE",FACE,{"disambiguationData":[OSD([sQuery(id+"F0.wireOp",EDGE,"E4"),sQuery(id+"F0.wireOp",EDGE,"E5"),sQuery(id+"F0.wireOp",EDGE,"E6"),sQuery(id+"F0.wireOp",EDGE,"E7"),sQuery(id+"F0.wireOp",EDGE,"E8.bottom"),sQuery(id+"F0.wireOp",EDGE,"E8.top"),sQuery(id+"F0.wireOp",EDGE,"E8.left"),sQuery(id+"F0.wireOp",EDGE,"E8.right"),subQ0])],"isStart":false}),makeQuery(id+"F1.opExtrude","SWEPT_FACE",FACE,{"disambiguationData":[OSD([subQ0])]}),makeQuery(id+"F4.opExtrude","SWEPT_FACE",FACE,{"disambiguationData":[OSD([sQuery(id+"F3.wireOp",EDGE,"E16")])]}),makeQuery(id+"F6.boolean.opBoolean","COPY",FACE,{"derivedFrom":makeQuery(id+"F6.opExtrude","SWEPT_FACE",FACE,{"disambiguationData":[OSD([sQuery(id+"F5.wireOp",EDGE,"E26")])]})}),makeQuery(id+"F6.boolean.opBoolean","COPY",FACE,{"derivedFrom":makeQuery(id+"F6.opExtrude","SWEPT_FACE",FACE,{"disambiguationData":[OSD([sQuery(id+"F5.wireOp",EDGE,"E31.MirrorCS")])]})})])],"derivedFrom":makeQuery(id+"F1.opExtrude","CAP_EDGE",EDGE,{"disambiguationData":[OSD([subQ0])],"isStart":false})});}
            var Q4;
            Q4=makeQuery(id+"F10.opFillet","BLEND_EDGE",EDGE,{"blendedFrom":[makeQuery(id+"F7.opPattern","COPY",EDGE,{"derivedFrom":makeQuery(id+"F6.boolean.opBoolean","INTERSECT",EDGE,{"derivedFrom":[makeQuery(id+"F4.opExtrude","SWEPT_FACE",FACE,{"disambiguationData":[OSD([sQuery(id+"F3.wireOp",EDGE,"E12")])]}),makeQuery(id+"F6.opExtrude","SWEPT_FACE",FACE,{"disambiguationData":[OSD([sQuery(id+"F5.wireOp",EDGE,"E31.MirrorCS")])]})]}),"instanceName":"1"}),makeQuery(id+"F9.boolean.opBoolean","MERGE",FACE,{"derivedFrom":[makeQuery(id+"F1.opExtrude","SWEPT_FACE",FACE,{"disambiguationData":[OSD([sQuery(id+"F0.wireOp",EDGE,"E9")])]}),makeQuery(id+"F9.opExtrude","SWEPT_FACE",FACE,{"disambiguationData":[OSD([sQuery(id+"F8.wireOp",EDGE,"E35")])]})]})],"blendedInto":[makeQuery(id+"F9.boolean.opBoolean","MERGE",FACE,{"derivedFrom":[makeQuery(id+"F1.opExtrude","SWEPT_FACE",FACE,{"disambiguationData":[OSD([sQuery(id+"F0.wireOp",EDGE,"E9")])]}),makeQuery(id+"F9.opExtrude","SWEPT_FACE",FACE,{"disambiguationData":[OSD([sQuery(id+"F8.wireOp",EDGE,"E35")])]})]})]});
            var Q5;
            Q5=makeQuery(id+"F9.boolean.opBoolean","INTERSECT",EDGE,{"derivedFrom":[makeQuery(id+"F7.opPattern","COPY",FACE,{"derivedFrom":makeQuery(id+"F6.boolean.opBoolean","SPLIT",FACE,{"disambiguationData":[TD([makeQuery(id+"F6.opExtrude","SWEPT_FACE",FACE,{"disambiguationData":[OSD([sQuery(id+"F5.wireOp",EDGE,"E24.MirrorCS")])]})])],"derivedFrom":makeQuery(id+"F4.opExtrude","SWEPT_FACE",FACE,{"disambiguationData":[OSD([sQuery(id+"F3.wireOp",EDGE,"E12")])]})}),"instanceName":"1"}),makeQuery(id+"F9.opExtrude","SWEPT_FACE",FACE,{"disambiguationData":[OSD([sQuery(id+"F8.wireOp",EDGE,"E35")])]})]});
            var Q6;
            Q6=makeQuery(id+"F9.boolean.opBoolean","INTERSECT",EDGE,{"derivedFrom":[makeQuery(id+"F7.opPattern","COPY",FACE,{"derivedFrom":makeQuery(id+"F6.boolean.opBoolean","COPY",FACE,{"derivedFrom":makeQuery(id+"F6.opExtrude","SWEPT_FACE",FACE,{"disambiguationData":[OSD([sQuery(id+"F5.wireOp",EDGE,"E31.MirrorCS")])]})}),"instanceName":"1"}),makeQuery(id+"F9.opExtrude","SWEPT_FACE",FACE,{"disambiguationData":[OSD([sQuery(id+"F8.wireOp",EDGE,"E35")])]})]});
            var Q7;
            {var subQ0=sQuery(id+"F0.wireOp",EDGE,"E9");var subQ1=makeQuery(id+"F1.opExtrude","SWEPT_FACE",FACE,{"disambiguationData":[OSD([subQ0])]});var subQ2=makeQuery(id+"F6.opExtrude","SWEPT_FACE",FACE,{"disambiguationData":[OSD([sQuery(id+"F5.wireOp",EDGE,"E31.MirrorCS")])]});var subQ4=sQuery(id+"F3.wireOp",EDGE,"E10");var subQ5=makeQuery(id+"F4.opExtrude","SWEPT_FACE",FACE,{"disambiguationData":[OSD([subQ4])]});var subQ17=sQuery(id+"F0.wireOp",EDGE,"E8.top");Q7=makeQuery(id+"F11.opFillet","BLEND_EDGE",EDGE,{"blendedFrom":[makeQuery(id+"F10.opFillet","BLEND_EDGE",EDGE,{"blendedFrom":[makeQuery(id+"F7.opPattern","COPY",EDGE,{"derivedFrom":makeQuery(id+"F6.boolean.opBoolean","INTERSECT",EDGE,{"derivedFrom":[subQ5,subQ2]}),"instanceName":"1"}),makeQuery(id+"F7.boolean.opBoolean","SPLIT",FACE,{"disambiguationData":[TD([makeQuery(id+"F1.opExtrude","SWEPT_FACE",FACE,{"disambiguationData":[OSD([subQ17])]})])],"derivedFrom":makeQuery(id+"F1.opExtrude","CAP_FACE",FACE,{"disambiguationData":[OSD([sQuery(id+"F0.wireOp",EDGE,"E4"),sQuery(id+"F0.wireOp",EDGE,"E5"),sQuery(id+"F0.wireOp",EDGE,"E6"),sQuery(id+"F0.wireOp",EDGE,"E7"),sQuery(id+"F0.wireOp",EDGE,"E8.bottom"),subQ17,sQuery(id+"F0.wireOp",EDGE,"E8.left"),sQuery(id+"F0.wireOp",EDGE,"E8.right"),subQ0])],"isStart":false})})],"blendedInto":[makeQuery(id+"F7.boolean.opBoolean","SPLIT",FACE,{"disambiguationData":[TD([makeQuery(id+"F1.opExtrude","SWEPT_FACE",FACE,{"disambiguationData":[OSD([subQ17])]})])],"derivedFrom":makeQuery(id+"F1.opExtrude","CAP_FACE",FACE,{"disambiguationData":[OSD([sQuery(id+"F0.wireOp",EDGE,"E4"),sQuery(id+"F0.wireOp",EDGE,"E5"),sQuery(id+"F0.wireOp",EDGE,"E6"),sQuery(id+"F0.wireOp",EDGE,"E7"),sQuery(id+"F0.wireOp",EDGE,"E8.bottom"),subQ17,sQuery(id+"F0.wireOp",EDGE,"E8.left"),sQuery(id+"F0.wireOp",EDGE,"E8.right"),subQ0])],"isStart":false})})]}),makeQuery(id+"F9.boolean.opBoolean","MERGE",FACE,{"derivedFrom":[subQ1,makeQuery(id+"F9.opExtrude","SWEPT_FACE",FACE,{"disambiguationData":[OSD([sQuery(id+"F8.wireOp",EDGE,"E35")])]})]})],"blendedInto":[makeQuery(id+"F9.boolean.opBoolean","MERGE",FACE,{"derivedFrom":[subQ1,makeQuery(id+"F9.opExtrude","SWEPT_FACE",FACE,{"disambiguationData":[OSD([sQuery(id+"F8.wireOp",EDGE,"E35")])]})]})]});}
            var Q8;
            Q8=makeQuery(id+"F9.boolean.opBoolean","INTERSECT",EDGE,{"derivedFrom":[makeQuery(id+"F7.opPattern","COPY",FACE,{"derivedFrom":makeQuery(id+"F6.boolean.opBoolean","COPY",FACE,{"derivedFrom":makeQuery(id+"F6.opExtrude","SWEPT_FACE",FACE,{"disambiguationData":[OSD([sQuery(id+"F5.wireOp",EDGE,"E26")])]})}),"instanceName":"1"}),makeQuery(id+"F9.opExtrude","SWEPT_FACE",FACE,{"disambiguationData":[OSD([sQuery(id+"F8.wireOp",EDGE,"E35")])]})]});
            var Q9;
            Q9=makeQuery(id+"F9.boolean.opBoolean","INTERSECT",EDGE,{"derivedFrom":[makeQuery(id+"F6.boolean.opBoolean","COPY",FACE,{"derivedFrom":makeQuery(id+"F6.opExtrude","SWEPT_FACE",FACE,{"disambiguationData":[OSD([sQuery(id+"F5.wireOp",EDGE,"E26")])]})}),makeQuery(id+"F9.opExtrude","SWEPT_FACE",FACE,{"disambiguationData":[OSD([sQuery(id+"F8.wireOp",EDGE,"E35")])]})]});
            var Q10;
            Q10=makeQuery(id+"F9.boolean.opBoolean","INTERSECT",EDGE,{"derivedFrom":[makeQuery(id+"F6.boolean.opBoolean","COPY",FACE,{"derivedFrom":makeQuery(id+"F6.opExtrude","SWEPT_FACE",FACE,{"disambiguationData":[OSD([sQuery(id+"F5.wireOp",EDGE,"E31.MirrorCS")])]})}),makeQuery(id+"F9.opExtrude","SWEPT_FACE",FACE,{"disambiguationData":[OSD([sQuery(id+"F8.wireOp",EDGE,"E35")])]})]});
            fillet(context, id + "F18", {"entities" : qUnion([Q0, Q1, Q2, Q3, Q4, Q5, Q6, Q7, Q8, Q9, Q10]), "radius" : 2 * mm, "tangentPropagation" : true, "allowEdgeOverflow" : false});
        }
    });
